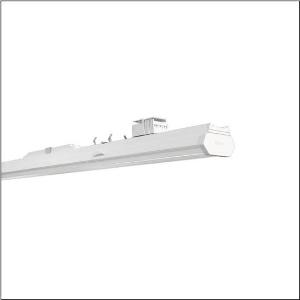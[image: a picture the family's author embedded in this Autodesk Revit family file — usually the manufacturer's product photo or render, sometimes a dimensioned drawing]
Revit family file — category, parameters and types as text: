
# Revit family: licross_r__11_protected_ho_51td1bdn4e5m3s_7495
name_source: partatom
category: Lighting Fixtures
units: mm (PartAtom-declared; Revit-internal decimal feet)

## family parameters
Cut with Voids When Loaded = No
Host = Face
Light Source = No
Part Type = Normal
Room Calculation Point = No
Round Connector Dimension = Use Diameter
Shared = No

## types (1)
- --- (1 x LED, 920 lm, 7.4 W, 4000K)
    Apparent Load = 7 VA
    CIE Flux Codes = 54 82 95 97 100
    Color Rendering = 80
    Color Temperature = 4000K
    Default Elevation = 1800 mm
    Description = Licross® 11 Protected HO, luminaire insert, of sheet steel, galvanised, coil coated, white, length: 1.500mm, width: 90mm, height: 101mm, LED rated luminous flux: 14.500lm, light colour: 840, control gear: DALI 2 (for two DALI lines), with plug, 6-pole, with phase selection, for trunking rail, 14-core, mains connection: 220..240V, AC, 50/60Hz, rated input power: 91W, for trunking rail, 14-core, halogen-free wiring, for emergency light function, converter,control gear: single battery element, battery: LiFePO4, 9Ah, primary optical cover: cover, of PMMA, light emission: direct distribution, primary light characteristic: symmetric, protection rating (complete): IP54, insulation class (complete): insulation class I (protective earthing), certification: CE, UKCA, protection symbol: D if used in an environment with non-conductive dust loads with corresponding accessories, impact resistance: IK06, permissible ambient temperature for indoor applications: +5..+30°C, standard: EN 60598-2-22, LABS conformity tested according to VDMA 24364:2018-05, reducing of maximum allowable ambient temperature of 5°C with ceiling mounting, corresponds to IFS (International Featured Standards) requirements for safety and quality in the food industry, packaging unit: 1 piece
    Height = 92 mm
    Lamp = 1 x LED
    Lamp Light Flux = 920 lm
    Lamp Power = 7.4 W
    Lamp count = 1
    Length = 1500 mm
    Luminous efficacy = 124 lm/W
    Manufacturer = Siteco
    ModVariant = No
    Model = 51TD1BDN4E5M3S
    Mounting Place = Ceiling
    Mounting Type = Pendant
    Number of Poles = 1
    OnlyDefault = Yes
    Power Factor = 1
    Product Name = Licross® 11 Protected HO
    Product group = luminaire insert
    ProductGroupID = 901
    Protection Class = Protection class I
    Protection Degree = IP 54
    RLX_Detail_Level = 1
    RLX_Emergency_Light_Flux = 0 lm
    RLX_Emergency_Type = 0
    RLX_Emergency_Type_DB = No
    RlxData = <blob elided: 24709 chars, md5=c6167f5e>
    Socket = socket
    Standby Power = 0 W
    System Light Flux = 920 lm
    System Power = 7 W
    Type Comments = : emergency light operation: 3 h
    Type Image = l_1256145.jpg
    URL = http://relux.com
    VarID = @adj_060103
    Voltage = 0 V
    Weight = 0.00 kg
    Width = 88 mm

## geometry (parser evidence)
native form markers: Blend x4, Sweep x12
no freeform markers — native parametric forms only
